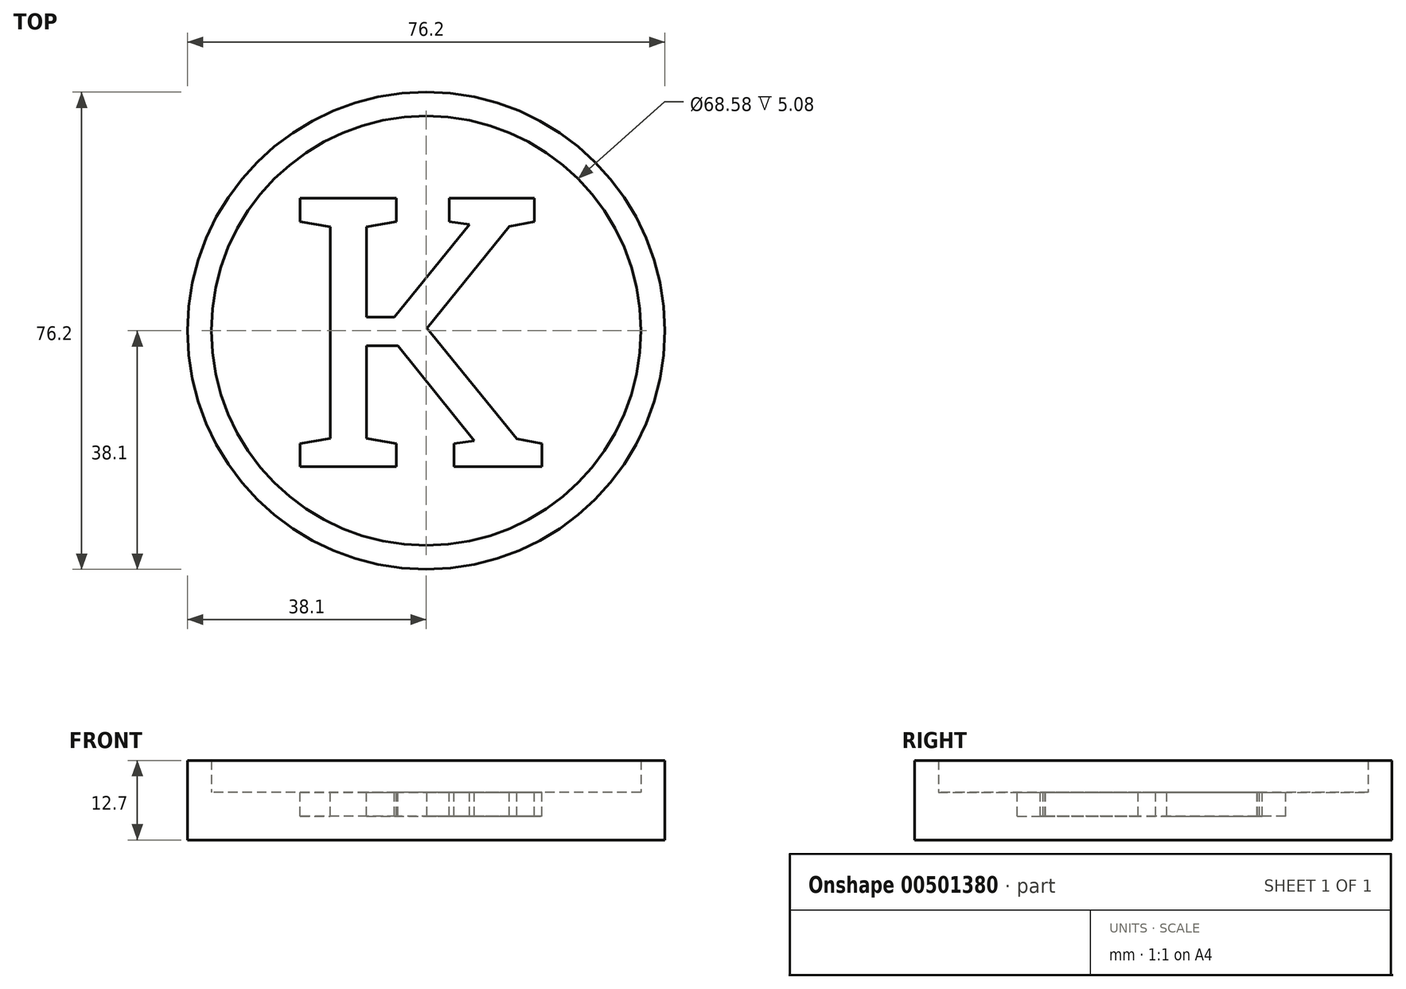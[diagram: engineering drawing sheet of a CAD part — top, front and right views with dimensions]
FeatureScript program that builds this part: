
annotation { "Feature Type Name" : "Feature", "Feature Type Description" : "" }
export const myFeature = defineFeature(function(context is Context, id is Id, definition is map)
    precondition{}
    {
        {
            var Q0;
            Q0=qCreatedBy(makeId("Top.planeOp"),FACE);
            var sketch = newSketch(context, id + "F0", { "sketchPlane" : qUnion([Q0])});
            skCircle(sketch, "E0", {"center": v(0, 0) * mm, "radius": 38.1 * mm});
            skSolve(sketch);
        }
        {
            var Q0;
            Q0=makeQuery(id+"F0.imprint","IMPRINT",FACE,{"disambiguationData":[TD([[makeQuery(id+"F0.imprint","IMPRINT",EDGE,{"derivedFrom":sQuery(id+"F0.wireOp",EDGE,"E0")}),1.0]])]});
            extrude(context, id + "F1", {"entities" : qUnion([Q0]), "depth" : 7.62 * mm});
        }
        {
            var Q0;
            Q0=makeQuery(id+"F1.opExtrude","CAP_FACE",FACE,{"disambiguationData":[OSD([sQuery(id+"F0.wireOp",EDGE,"E0")])],"isStart":false});
            var sketch = newSketch(context, id + "F2", { "sketchPlane" : qUnion([Q0])});
            skCircle(sketch, "E1", {"center": v(0, 0) * mm, "radius": 38.1 * mm});
            skCircle(sketch, "E2", {"center": v(0, 0) * mm, "radius": 34.3 * mm});
            skSolve(sketch);
        }
        {
            var Q0;
            Q0=makeQuery(id+"F2.imprint","IMPRINT",FACE,{"disambiguationData":[TD([[makeQuery(id+"F2.imprint","IMPRINT",EDGE,{"derivedFrom":sQuery(id+"F2.wireOp",EDGE,"E1")}),1.0]])]});
            extrude(context, id + "F3", {"entities" : qUnion([Q0]), "operationType" : NewBodyOperationType.ADD, "depth" : 5.08 * mm});
        }
        {
            var Q0;
            Q0=makeQuery(id+"F1.opExtrude","CAP_FACE",FACE,{"disambiguationData":[OSD([sQuery(id+"F0.wireOp",EDGE,"E0")])],"isStart":false});
            var sketch = newSketch(context, id + "F4", { "sketchPlane" : qUnion([Q0])});
            skText(sketch, "E3", { "text": "K", "fontName": "RobotoSlab-Regular.ttf"});
            skLineSegment(sketch, "E4", {"start": v(0, 0) * mm, "end": v(22.23, 0) * mm, "construction": true});
            skLineSegment(sketch, "E5", {"start": v(22.23, 0) * mm, "end": v(22.23, 21.7) * mm, "construction": true});
            const initialGuessF4  = {"E3": [-0.02222, -0.02171, 1, 0, 0.0434]};
            skSetInitialGuess(sketch, initialGuessF4);
            skSolve(sketch);
        }
        {
            var Q0;
            Q0=makeQuery(id+"F4.imprint","IMPRINT",FACE,{"disambiguationData":[TD([[makeQuery(id+"F4.imprint","IMPRINT",EDGE,{"derivedFrom":sQuery(id+"F4.wireOp",EDGE,"E3.sketch_text.stroke-0")}),-1.0]])]});
            extrude(context, id + "F5", {"entities" : qUnion([Q0]), "operationType" : NewBodyOperationType.REMOVE, "oppositeDirection" : true, "depth" : 3.8 * mm});
        }
    });
